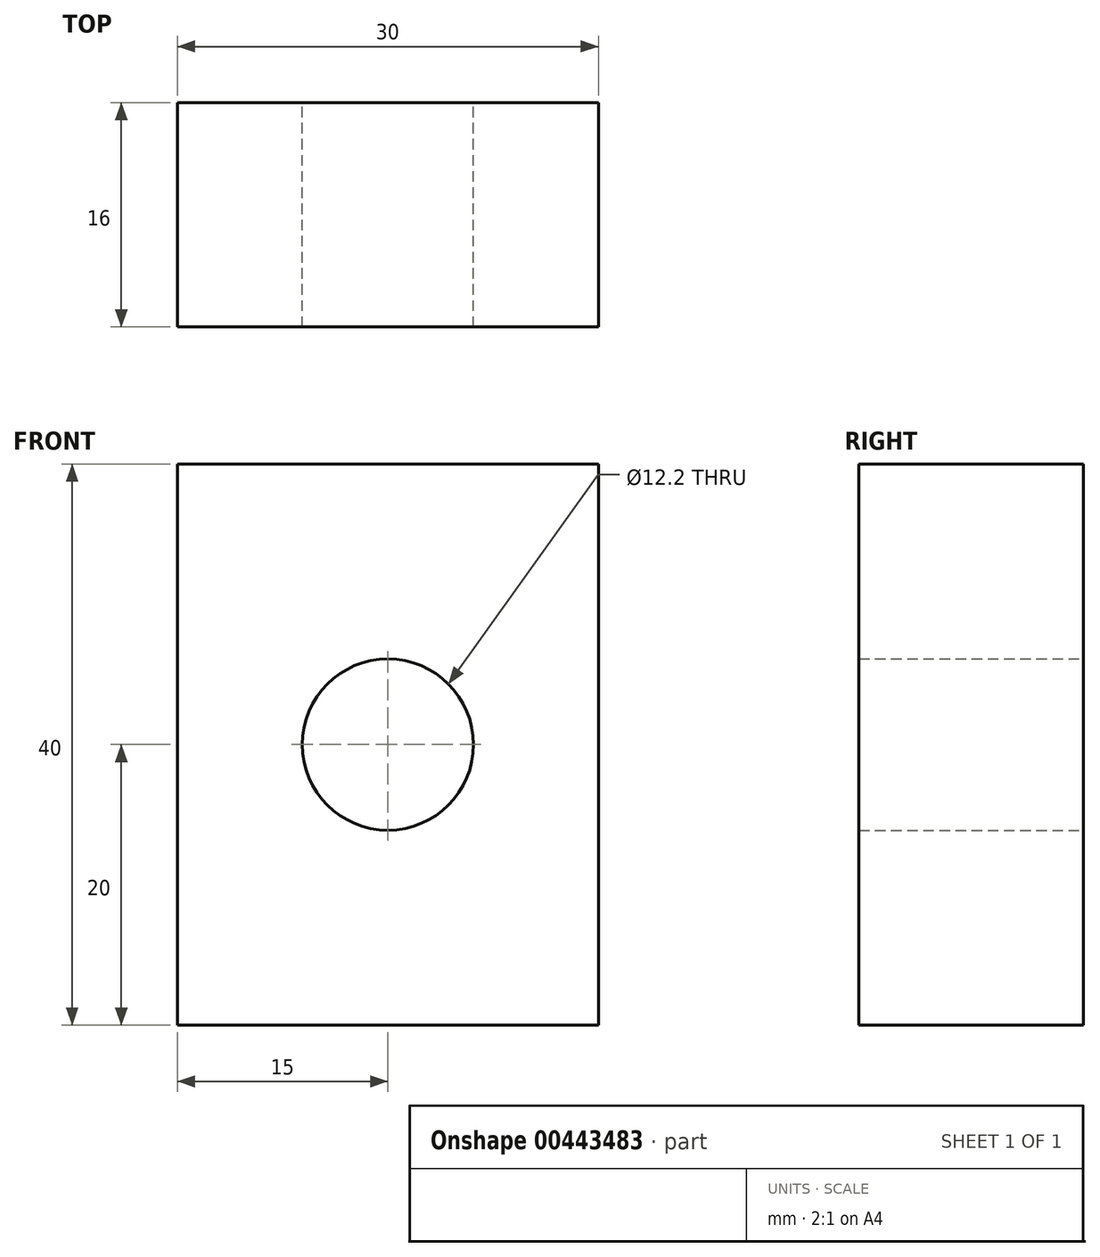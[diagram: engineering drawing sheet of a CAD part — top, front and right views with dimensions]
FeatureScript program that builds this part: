
annotation { "Feature Type Name" : "Feature", "Feature Type Description" : "" }
export const myFeature = defineFeature(function(context is Context, id is Id, definition is map)
    precondition{}
    {
        {
            var Q0;
            Q0=qCreatedBy(makeId("Front.planeOp"),FACE);
            var sketch = newSketch(context, id + "F0", { "sketchPlane" : qUnion([Q0])});
            skLineSegment(sketch, "E0.bottom", {"start": v(-15, 20) * mm, "end": v(15, 20) * mm});
            skLineSegment(sketch, "E0.top", {"start": v(-15, -20) * mm, "end": v(15, -20) * mm});
            skLineSegment(sketch, "E0.left", {"start": v(-15, 20) * mm, "end": v(-15, -20) * mm});
            skLineSegment(sketch, "E0.right", {"start": v(15, 20) * mm, "end": v(15, -20) * mm});
            skPoint(sketch, "E1", {"position": v(0, 0) * mm});
            skSolve(sketch);
        }
        {
            var Q0;
            Q0 = qSketchRegion(id + "F0", true);
            extrude(context, id + "F1", {"entities" : qUnion([Q0]), "depth" : 16 * mm, "offsetDistance" : 25 * mm});
        }
        {
            var Q0;
            Q0=makeQuery(id+"F1.opExtrude","CAP_FACE",FACE,{"disambiguationData":[OSD([sQuery(id+"F0.wireOp",EDGE,"E0.bottom"),sQuery(id+"F0.wireOp",EDGE,"E0.top"),sQuery(id+"F0.wireOp",EDGE,"E0.left"),sQuery(id+"F0.wireOp",EDGE,"E0.right")])],"isStart":true});
            var sketch = newSketch(context, id + "F2", { "sketchPlane" : qUnion([Q0])});
            skPoint(sketch, "E2", {"position": v(0, 0) * mm});
            skSolve(sketch);
        }
        {
            var Q0;
            Q0=sQuery(id+"F2.wireOp",VERTEX,"E2");
            var Q1;
            Q1=makeQuery(id+"F1.opExtrude","SWEPT_BODY",BODY,{"disambiguationData":[OSD([sQuery(id+"F0.wireOp",EDGE,"E0.bottom"),sQuery(id+"F0.wireOp",EDGE,"E0.top"),sQuery(id+"F0.wireOp",EDGE,"E0.left"),sQuery(id+"F0.wireOp",EDGE,"E0.right")])]});
            hole(context, id + "F3", {"style" : HoleStyle.C_SINK, "endStyle" : HoleEndStyle.BLIND, "holeDiameter" : 12.2 * mm, "cSinkDiameter" : 12.2 * mm, "cSinkAngle" : 90 * degree, "majorDiameter" : 5 * mm, "holeDepth" : 60 * mm, "isTappedThrough" : true, "tappedDepth" : 12 * mm, "tapClearance" : 3, "locations" : qUnion([Q0]), "scope" : qUnion([Q1])});
        }
    });
